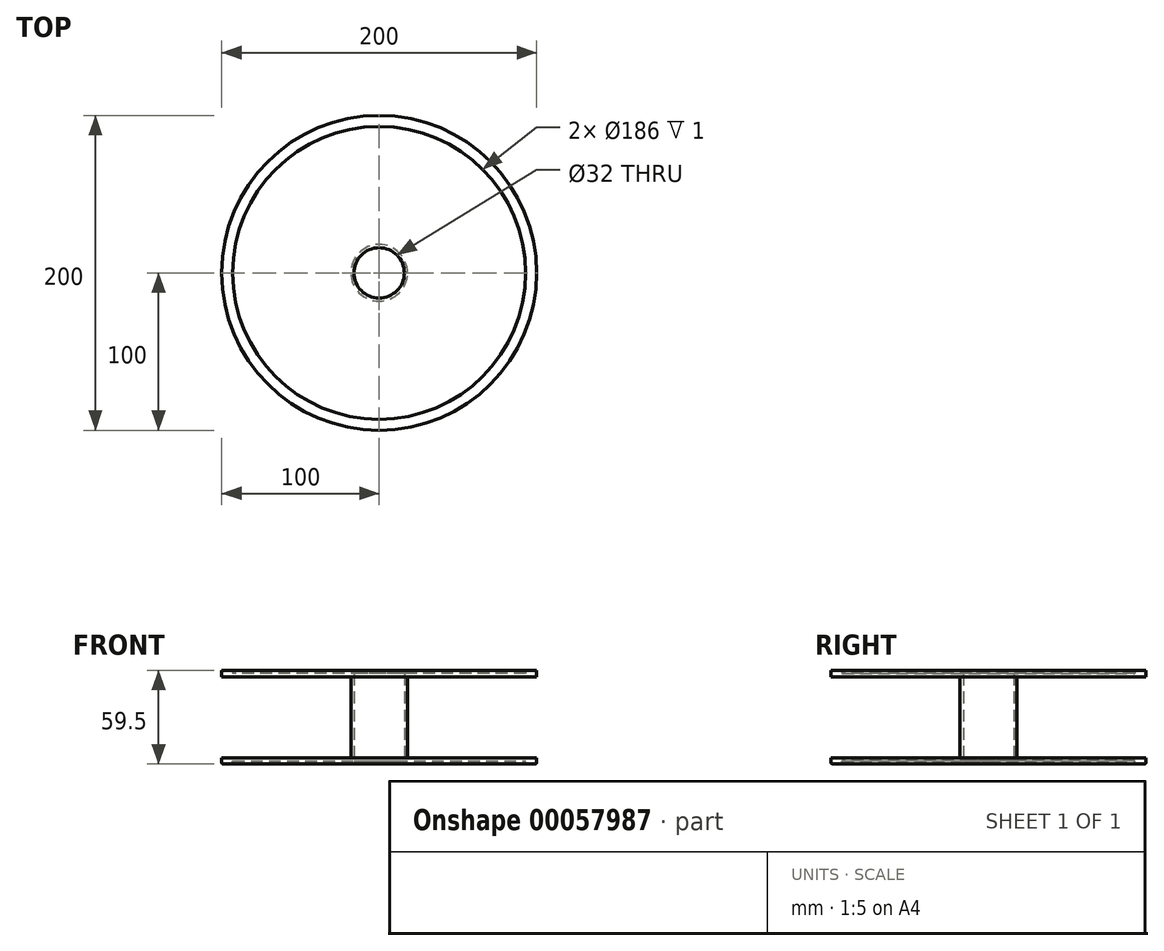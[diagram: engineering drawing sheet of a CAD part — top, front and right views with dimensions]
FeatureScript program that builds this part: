
annotation { "Feature Type Name" : "Feature", "Feature Type Description" : "" }
export const myFeature = defineFeature(function(context is Context, id is Id, definition is map)
    precondition{}
    {
        {
            var Q0;
            Q0=qCreatedBy(makeId("Top.planeOp"),FACE);
            var sketch = newSketch(context, id + "F0", { "sketchPlane" : qUnion([Q0])});
            skCircle(sketch, "E0", {"center": v(0, 0) * mm, "radius": 100 * mm});
            skSolve(sketch);
        }
        {
            var Q0;
            Q0=qSketchRegion(id+"F0",true);
            extrude(context, id + "F1", {"entities" : qUnion([Q0]), "depth" : 2 * mm});
        }
        {
            var Q0;
            Q0=makeQuery(id+"F1.opExtrude","CAP_FACE",FACE,{"disambiguationData":[OSD([sQuery(id+"F0.wireOp",EDGE,"E0")])],"isStart":false});
            var sketch = newSketch(context, id + "F2", { "sketchPlane" : qUnion([Q0])});
            skCircle(sketch, "E1.0", {"center": v(0, 0) * mm, "radius": 100 * mm});
            skCircle(sketch, "E1.1", {"center": v(0, 0) * mm, "radius": 100 * mm});
            skCircle(sketch, "E2", {"center": v(0, 0) * mm, "radius": 93 * mm});
            skSolve(sketch);
        }
        {
            var Q0;
            Q0=qSketchRegion(id+"F2",true);
            extrude(context, id + "F3", {"entities" : qUnion([Q0]), "operationType" : NewBodyOperationType.ADD, "depth" : 2 * mm});
        }
        {
            var Q0;
            Q0=makeQuery(id+"F1.opExtrude","CAP_FACE",FACE,{"disambiguationData":[OSD([sQuery(id+"F0.wireOp",EDGE,"E0")])],"isStart":true});
            var sketch = newSketch(context, id + "F4", { "sketchPlane" : qUnion([Q0])});
            skCircle(sketch, "E3", {"center": v(0, 0) * mm, "radius": 18 * mm});
            skSolve(sketch);
        }
        {
            var Q0;
            Q0=qSketchRegion(id+"F4",true);
            extrude(context, id + "F5", {"entities" : qUnion([Q0]), "operationType" : NewBodyOperationType.ADD, "depth" : 51.5 * mm});
        }
        {
            var Q0;
            Q0=makeQuery(id+"F5.opExtrude","CAP_FACE",FACE,{"disambiguationData":[OSD([sQuery(id+"F4.wireOp",EDGE,"E3")])],"isStart":false});
            var sketch = newSketch(context, id + "F6", { "sketchPlane" : qUnion([Q0])});
            skCircle(sketch, "E4.0", {"center": v(0, 0) * mm, "radius": 100 * mm});
            skSolve(sketch);
        }
        {
            var Q0;
            Q0=qSketchRegion(id+"F6",true);
            extrude(context, id + "F7", {"entities" : qUnion([Q0]), "operationType" : NewBodyOperationType.ADD, "depth" : 2 * mm});
        }
        {
            var Q0;
            Q0=makeQuery(id+"F7.opExtrude","CAP_FACE",FACE,{"disambiguationData":[OSD([sQuery(id+"F6.wireOp",EDGE,"E4.0")])],"isStart":false});
            var sketch = newSketch(context, id + "F8", { "sketchPlane" : qUnion([Q0])});
            skCircle(sketch, "E5", {"center": v(0, 0) * mm, "radius": 93 * mm});
            skCircle(sketch, "E6.0", {"center": v(0, 0) * mm, "radius": 100 * mm});
            skSolve(sketch);
        }
        {
            var Q0;
            Q0=qSketchRegion(id+"F8",true);
            extrude(context, id + "F9", {"entities" : qUnion([Q0]), "operationType" : NewBodyOperationType.ADD, "depth" : 2 * mm});
        }
        {
            var Q0;
            Q0=makeQuery(id+"F3.opExtrude","CAP_EDGE",EDGE,{"disambiguationData":[OSD([sQuery(id+"F2.wireOp",EDGE,"E2")])],"isStart":false});
            var Q1;
            Q1=makeQuery(id+"F3.opExtrude","CAP_EDGE",EDGE,{"disambiguationData":[OSD([sQuery(id+"F2.wireOp",EDGE,"E1.1")])],"isStart":false});
            var Q2;
            Q2=makeQuery(id+"F9.opExtrude","CAP_EDGE",EDGE,{"disambiguationData":[OSD([sQuery(id+"F8.wireOp",EDGE,"E5")])],"isStart":false});
            var Q3;
            Q3=makeQuery(id+"F9.opExtrude","CAP_EDGE",EDGE,{"disambiguationData":[OSD([sQuery(id+"F8.wireOp",EDGE,"E6.0")])],"isStart":false});
            fillet(context, id + "F10", {"entities" : qUnion([Q0, Q1, Q2, Q3]), "radius" : 1 * mm, "tangentPropagation" : true, "allowEdgeOverflow" : false});
        }
        {
            var Q0;
            Q0=makeQuery(id+"F7.opExtrude","CAP_FACE",FACE,{"disambiguationData":[OSD([sQuery(id+"F6.wireOp",EDGE,"E4.0")])],"isStart":false});
            var sketch = newSketch(context, id + "F11", { "sketchPlane" : qUnion([Q0])});
            skCircle(sketch, "E7", {"center": v(0, 0) * mm, "radius": 16 * mm});
            skSolve(sketch);
        }
        {
            var Q0;
            Q0=qSketchRegion(id+"F11",true);
            extrude(context, id + "F12", {"entities" : qUnion([Q0]), "operationType" : NewBodyOperationType.REMOVE, "oppositeDirection" : true, "depth" : 69 * mm});
        }
    });
